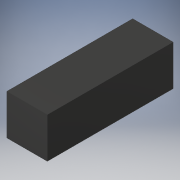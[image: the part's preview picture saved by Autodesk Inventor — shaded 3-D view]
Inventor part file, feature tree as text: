
AUTODESK INVENTOR PART (.ipt)
format: ipt  version: 2019 (Build 230136000, 136)  size: 135,680 bytes
history: native  units: mm
features: sketch x5, extrude x4
ambient origin geometry x8: Origin, YZ Plane, XZ Plane, XY Plane, X Axis, Y Axis, Z Axis, Center Point
bodies: Solid1 (feature_tree)
feature tree (9):
  extrude  "Extrusion1"  Depth=22.5mm
  extrude  "Extrusion2"  Depth=2.0mm
  extrude  "Extrusion3"  Depth=20.5mm
  sketch  "Sketch4"  dims[d6=20.5mm d7=2.0mm]
  extrude  "Extrusion4"  Depth=2.0mm
  sketch  "Sketch1"  dims[d0=22.5mm d1=22.5mm]
  sketch  "Sketch2"  dims[d2=20.5mm d3=2.0mm]
  sketch  "Sketch3"  dims[d4=2.0mm d5=20.5mm]
  sketch  "Sketch5"  dims[d8=2.0mm d9=20.5mm d10=18.5mm d11=18.5mm d12=69.0mm d13=0.0mm d14=2.0mm d15=67.0mm d16=18.5mm d17=66.0mm d18=18.5mm d19=0.0mm d20=22.5mm d21=22.5mm d22=1.0mm d23=0.0mm d24=18.5mm d25=66.0mm d26=2.0mm d27=0.0mm]
